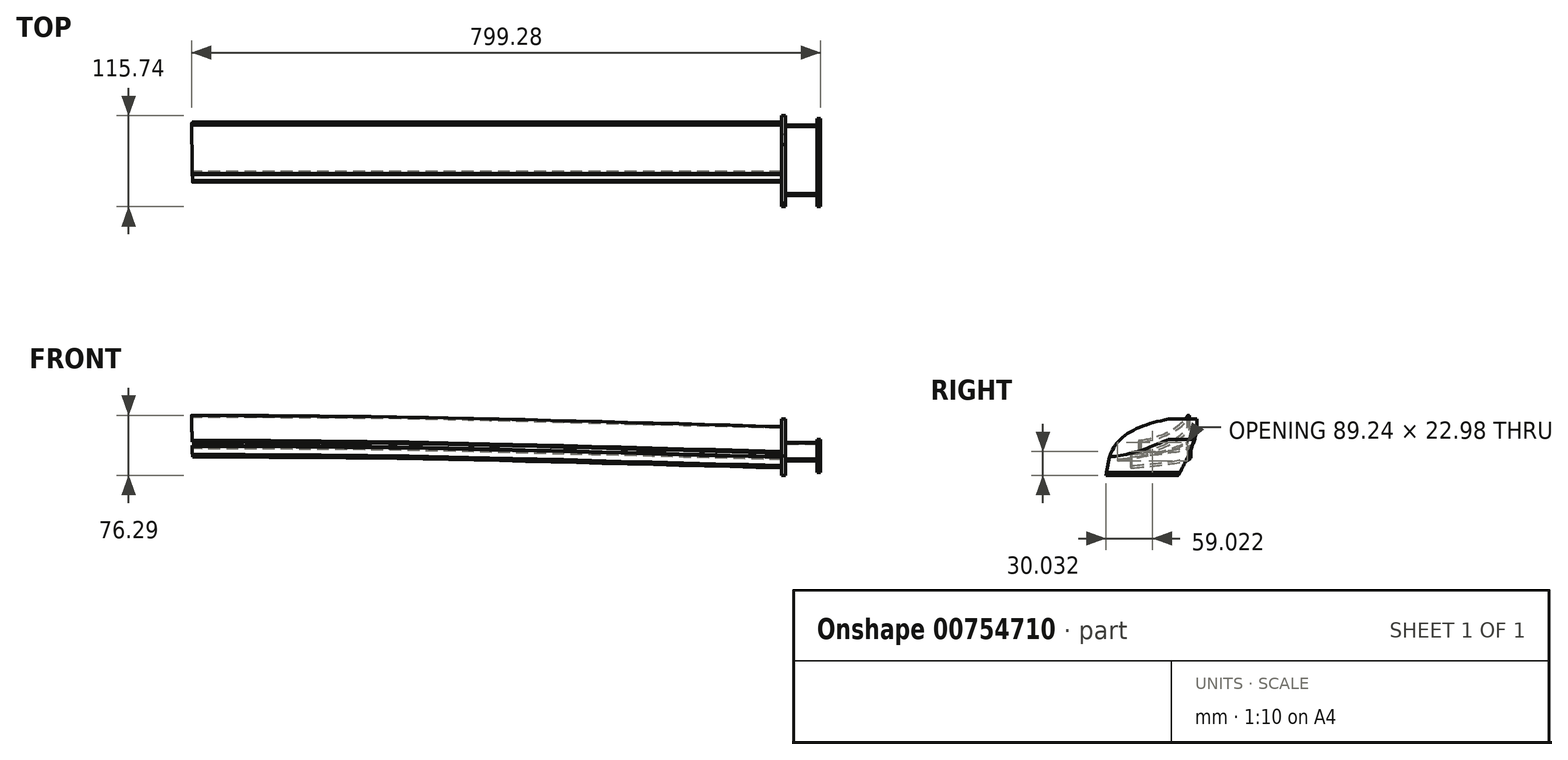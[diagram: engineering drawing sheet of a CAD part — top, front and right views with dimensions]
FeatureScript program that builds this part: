
annotation { "Feature Type Name" : "Feature", "Feature Type Description" : "" }
export const myFeature = defineFeature(function(context is Context, id is Id, definition is map)
    precondition{}
    {
        {
            var Q0;
            Q0=qCreatedBy(makeId("Right.planeOp"),FACE);
            cPlane(context, id + "F0", {"entities" : qUnion([Q0]), "cplaneType" : CPlaneType.OFFSET, "offset" : 750 * mm, "width" : 152.4 * mm, "height" : 152.4 * mm});
        }
        {
            var Q0;
            Q0=qCreatedBy(id+"F0.planeOp",FACE);
            var sketch = newSketch(context, id + "F1", { "sketchPlane" : qUnion([Q0])});
            skFitSpline(sketch, "E0", {"points": [v(-41.5, 9.77) * mm, v(-21.1, 14.02) * mm, v(10.34, 30.45) * mm, v(19.4, 40.65) * mm, v(19.69, 41.22) * mm], "startDerivative": vector(61.8, 8.42) * mm, "endDerivative": vector(3.22, 7.86) * mm});
            skFitSpline(sketch, "E1", {"points": [v(-39.2, 7.57) * mm, v(-18.8, 11.82) * mm, v(12.64, 28.25) * mm, v(21.7, 38.45) * mm, v(21.99, 39.02) * mm], "startDerivative": vector(61.8, 8.42) * mm, "endDerivative": vector(3.22, 7.86) * mm});
            skArc(sketch, "E2", {"start": v(21.99, 39.02) * mm, "mid": v(21.77, 41.1) * mm, "end": v(19.69, 41.22) * mm});
            skFitSpline(sketch, "E3", {"points": [v(-41.5, 9.77) * mm, v(-42.96, 8.52) * mm, v(-39.2, 7.57) * mm], "startDerivative": vector(-5.59, -3.32) * mm, "endDerivative": vector(9.32, -1.2) * mm});
            skSolve(sketch);
        }
        {
            var Q0;
            Q0=qCreatedBy(makeId("Front.planeOp"),FACE);
            var sketch = newSketch(context, id + "F2", { "sketchPlane" : qUnion([Q0])});
            skFitSpline(sketch, "E4", {"points": [v(748.5, 7.1) * mm, v(403.01, 16.27) * mm, v(238.6, 19.61) * mm, v(0, 21.28) * mm], "startDerivative": vector(-963.34, 26.03) * mm, "endDerivative": vector(-774.9, 3.66) * mm});
            skSolve(sketch);
        }
        {
            var Q0;
            Q0=makeQuery(id+"F1.imprint","IMPRINT",FACE,{"disambiguationData":[TD([[makeQuery(id+"F1.imprint","IMPRINT",EDGE,{"derivedFrom":sQuery(id+"F1.wireOp",EDGE,"E0")}),-1.0]])]});
            var Q1;
            Q1=sQuery(id+"F2.wireOp",EDGE,"E4");
            sweep(context, id + "F3", {"profiles" : qUnion([Q0]), "path" : qUnion([Q1])});
        }
        {
            var Q0;
            Q0=qCreatedBy(id+"F0.planeOp",FACE);
            var sketch = newSketch(context, id + "F4", { "sketchPlane" : qUnion([Q0])});
            skFitSpline(sketch, "E5", {"points": [v(-50.85, -8.07) * mm, v(-10.62, -4.1) * mm, v(17.7, 0.7) * mm, v(21.39, 2.12) * mm], "startDerivative": vector(85.86, 7.16) * mm, "endDerivative": vector(18.95, 9.27) * mm});
            skFitSpline(sketch, "E6", {"points": [v(-50.85, -11.12) * mm, v(-10.62, -7.15) * mm, v(17.7, -2.34) * mm, v(21.39, -0.92) * mm], "startDerivative": vector(85.86, 7.16) * mm, "endDerivative": vector(18.95, 9.27) * mm});
            skFitSpline(sketch, "E7", {"points": [v(-50.85, -8.07) * mm, v(-52.56, -9.32) * mm, v(-52.18, -11.12) * mm, v(-50.85, -11.12) * mm], "startDerivative": vector(-6.02, -2.5) * mm, "endDerivative": vector(5.08, 1.42) * mm});
            skFitSpline(sketch, "E8", {"points": [v(21.39, 2.12) * mm, v(22.66, 3.26) * mm, v(23.82, 2.12) * mm, v(21.39, -0.92) * mm], "startDerivative": vector(4.02, 5.92) * mm, "endDerivative": vector(-8.7, -7.34) * mm});
            skSolve(sketch);
        }
        {
            var Q0;
            Q0=makeQuery(id+"F4.imprint","IMPRINT",FACE,{"disambiguationData":[TD([[makeQuery(id+"F4.imprint","IMPRINT",EDGE,{"derivedFrom":sQuery(id+"F4.wireOp",EDGE,"E5")}),-1.0]])]});
            var Q1;
            Q1=makeQuery(id+"F3.opSweep","SWEPT_EDGE",EDGE,{"disambiguationData":[OSD([sQuery(id+"F1.wireOp",EDGE,"E0"),sQuery(id+"F1.wireOp",EDGE,"E3"),sQuery(id+"F2.wireOp",EDGE,"E4")])]});
            sweep(context, id + "F5", {"profiles" : qUnion([Q0]), "path" : qUnion([Q1])});
        }
        {
            var Q0;
            Q0=qCreatedBy(id+"F0.planeOp",FACE);
            var sketch = newSketch(context, id + "F6", { "sketchPlane" : qUnion([Q0])});
            skLineSegment(sketch, "E9", {"start": v(-83.87, -20.54) * mm, "end": v(-79.17, 4.1) * mm});
            skLineSegment(sketch, "E10", {"start": v(-4.78, 51.13) * mm, "end": v(31.87, 51.13) * mm});
            skFitSpline(sketch, "E11", {"points": [v(31.87, 51.13) * mm, v(28.75, 25.92) * mm, v(8.07, -20.54) * mm], "startDerivative": vector(-1.58, -58.68) * mm, "endDerivative": vector(-43.7, -84.92) * mm});
            skLineSegment(sketch, "E12", {"start": v(-83.87, -20.54) * mm, "end": v(8.07, -20.54) * mm});
            skFitSpline(sketch, "E13", {"points": [v(-79.17, 4.1) * mm, v(-70.5, 19.69) * mm, v(-46.7, 38.1) * mm, v(-4.78, 51.13) * mm], "startDerivative": vector(26.6, 60.33) * mm, "endDerivative": vector(109.77, 25.93) * mm});
            skSolve(sketch);
        }
        {
            var Q0;
            Q0 = qSketchRegion(id + "F6", true);
            extrude(context, id + "F7", {"entities" : qUnion([Q0]), "depth" : 5 * mm, "offsetDistance" : 25 * mm});
        }
        {
            var Q0;
            Q0=makeQuery(id+"F7.opExtrude","CAP_FACE",FACE,{"disambiguationData":[OSD([sQuery(id+"F6.wireOp",EDGE,"E9"),sQuery(id+"F6.wireOp",EDGE,"hT4TQo0T-Fa7E-HjVr-Rcz7-hTDrzQASOiLT"),sQuery(id+"F6.wireOp",EDGE,"E10"),sQuery(id+"F6.wireOp",EDGE,"E11"),sQuery(id+"F6.wireOp",EDGE,"E12")])],"isStart":false});
            var sketch = newSketch(context, id + "F8", { "sketchPlane" : qUnion([Q0])});
            skFitSpline(sketch, "E14", {"points": [v(-67.42, 0) * mm, v(-47.87, 2.97) * mm, v(-2.26, 13.46) * mm, v(17.85, 20.82) * mm], "startDerivative": vector(59.75, 7.73) * mm, "endDerivative": vector(58.54, 24.61) * mm});
            skFitSpline(sketch, "E15", {"points": [v(-67.42, -2) * mm, v(-47.87, 0.97) * mm, v(-2.26, 11.46) * mm, v(17.85, 18.82) * mm], "startDerivative": vector(59.75, 7.73) * mm, "endDerivative": vector(58.54, 24.61) * mm});
            skFitSpline(sketch, "E16", {"points": [v(-67.42, 0) * mm, v(-69.47, -1.35) * mm, v(-67.42, -2) * mm], "startDerivative": vector(-6.09, -2.93) * mm, "endDerivative": vector(6.22, -1.04) * mm});
            skFitSpline(sketch, "E17", {"points": [v(17.85, 20.82) * mm, v(19.75, 20.82) * mm, v(19.37, 19.7) * mm, v(17.85, 18.82) * mm], "startDerivative": vector(6.97, 1.24) * mm, "endDerivative": vector(-4.8, -1.89) * mm});
            skSolve(sketch);
        }
        {
            var Q0;
            Q0 = qSketchRegion(id + "F8", true);
            extrude(context, id + "F9", {"entities" : qUnion([Q0]), "operationType" : NewBodyOperationType.ADD, "depth" : 40 * mm, "offsetDistance" : 25 * mm});
        }
        {
            var Q0;
            Q0=makeQuery(id+"F9.opExtrude","CAP_FACE",FACE,{"disambiguationData":[OSD([sQuery(id+"F8.wireOp",EDGE,"E14"),sQuery(id+"F8.wireOp",EDGE,"E15"),sQuery(id+"F8.wireOp",EDGE,"E16"),sQuery(id+"F8.wireOp",EDGE,"E17")])],"isStart":false});
            var sketch = newSketch(context, id + "F10", { "sketchPlane" : qUnion([Q0])});
            skLineSegment(sketch, "E18", {"start": v(-83.53, -16.85) * mm, "end": v(-79.85, 2.7) * mm});
            skFitSpline(sketch, "E19", {"points": [v(-79.85, 2.7) * mm, v(-47.84, 8.64) * mm, v(-16.96, 19.69) * mm, v(-5.35, 24.79) * mm], "startDerivative": vector(82.34, 11.41) * mm, "endDerivative": vector(42.43, 19.23) * mm});
            skLineSegment(sketch, "E20", {"start": v(-5.35, 24.79) * mm, "end": v(28.08, 24.79) * mm});
            skFitSpline(sketch, "E21", {"points": [v(28.08, 24.79) * mm, v(22.13, 8.07) * mm, v(9.95, -16.85) * mm], "startDerivative": vector(-11.5, -36) * mm, "endDerivative": vector(-24.3, -46.87) * mm});
            skLineSegment(sketch, "E22", {"start": v(-83.53, -16.85) * mm, "end": v(9.95, -16.85) * mm});
            skSolve(sketch);
        }
        {
            var Q0;
            Q0 = qSketchRegion(id + "F10", true);
            extrude(context, id + "F11", {"entities" : qUnion([Q0]), "operationType" : NewBodyOperationType.ADD, "depth" : 5 * mm, "offsetDistance" : 25 * mm});
        }
    });
